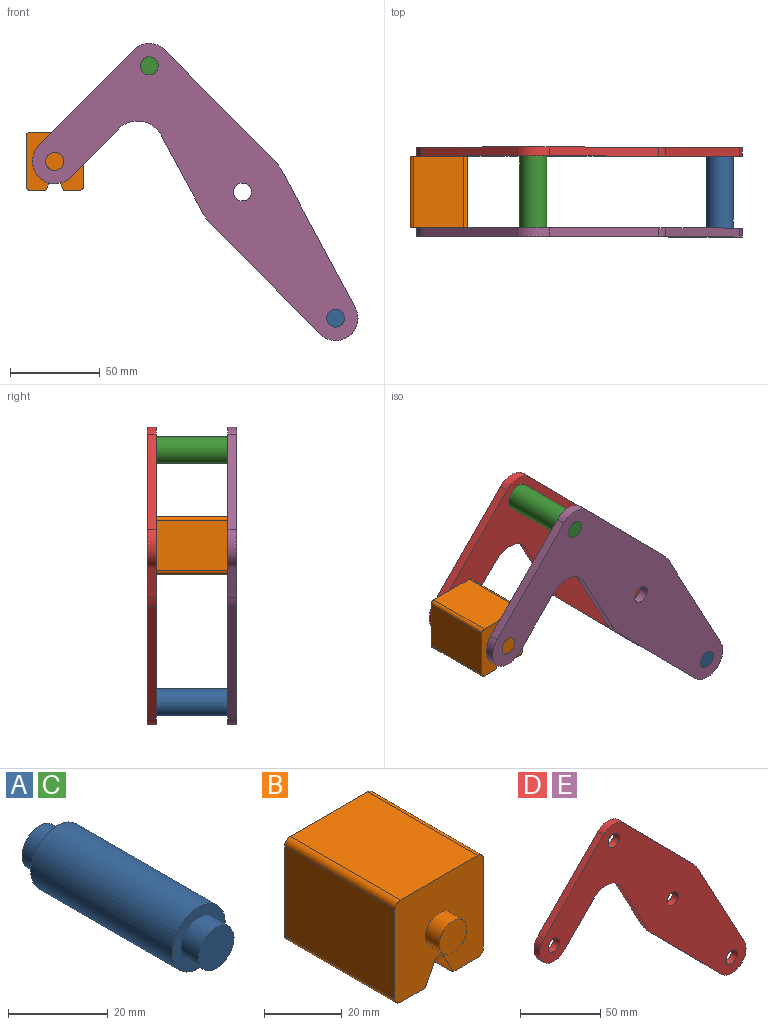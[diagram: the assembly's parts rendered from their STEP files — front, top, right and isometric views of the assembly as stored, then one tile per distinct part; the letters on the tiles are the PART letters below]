
ASSEMBLY  parts=5 mates=3
PART A: 7 faces, bbox 15x50x15 mm
  f0: cylinder r=7.5mm len=40mm, axis (0,-1,0), area 1885mm2, adj f2,f5
  f1: cylinder r=5mm len=10mm, axis (0,1,0), area 157.1mm2, adj f2,f3
  f2: plane 15x15mm, normal (0,-1,0), area 98.2mm2, adj f0,f1
  f3: plane 10x10mm, normal (0,-1,0), area 78.5mm2, adj f1
  f4: cylinder r=5mm len=10mm, axis (0,-1,0), area 157.1mm2, adj f5,f6
  f5: plane 15x15mm, normal (0,1,0), area 98.2mm2, adj f0,f4
  f6: plane 10x10mm, normal (0,1,0), area 78.5mm2, adj f4
PART B: 18 faces, bbox 32.1x50x32.1 mm
  f0: plane 40x28.08mm, normal (1,0,0), area 1123.1mm2, adj f4,f10,f13,f14
  f1: plane 40x9.04mm, normal (0,0,-1), area 361.6mm2, adj f2,f4,f10,f14
  f2: plane 40x6.42mm, normal (-0.89,0,-0.45), area 287.2mm2, adj f1,f4,f10,f15
  f3: plane 40x6.42mm, normal (0.89,0,-0.45), area 287.2mm2, adj f4,f5,f10,f15
  f4: plane 32.08x32.08mm, normal (0,-1,0), area 900.6mm2, adj f0,f1,f2,f3,f5,f6,f7,f9
  f5: plane 40x9.04mm, normal (0,0,-1), area 361.6mm2, adj f3,f4,f10,f16
  f6: plane 40x28.08mm, normal (0,0,1), area 1123.1mm2, adj f4,f10,f13,f17
  f7: plane 40x28.08mm, normal (-1,0,0), area 1123.1mm2, adj f4,f10,f16,f17
  f8: plane 10x10mm, normal (0,-1,0), area 78.5mm2, adj f9
  f9: cylinder r=5mm len=10mm, axis (0,1,0), area 157.1mm2, adj f4,f8
  f10: plane 32.08x32.08mm, normal (0,1,0), area 900.6mm2, adj f0,f1,f2,f3,f5,f6,f7,f12
  f11: plane 10x10mm, normal (0,1,0), area 78.5mm2, adj f12
  f12: cylinder r=5mm len=10mm, axis (0,-1,0), area 157.1mm2, adj f10,f11
  f13: cylinder r=2mm len=40mm, axis (0,1,0), area 125.7mm2, adj f0,f4,f6,f10
  f14: cylinder r=2mm len=40mm, axis (0,-1,0), area 125.7mm2, adj f0,f1,f4,f10
  f15: cylinder r=2mm len=40mm, axis (0,1,0), area 177.1mm2, adj f2,f3,f4,f10
  f16: cylinder r=2mm len=40mm, axis (0,1,0), area 125.7mm2, adj f4,f5,f7,f10
  f17: cylinder r=2mm len=40mm, axis (0,-1,0), area 125.7mm2, adj f4,f6,f7,f10
PART C: same geometry as A
PART D: 18 faces, bbox 181.7x5x165.8 mm
  f0: plane 43.49x23.35mm, normal (-0.88,0,-0.47), area 246.8mm2, adj f1,f14,f16,f17
  f1: cylinder r=25mm len=5.75mm, axis (0,1,0), area 35.8mm2, adj f0,f2,f16,f17
  f2: plane 61.6x60.87mm, normal (-0.71,0,-0.7), area 433mm2, adj f1,f3,f16,f17
  f3: cylinder r=12.5mm len=21.39mm, axis (0,1,0), area 178.4mm2, adj f2,f4,f16,f17
  f4: plane 76.3x40.96mm, normal (0.88,0,0.47), area 433mm2, adj f3,f5,f16,f17
  f5: cylinder r=25mm len=5.75mm, axis (0,1,0), area 35.8mm2, adj f4,f6,f16,f17
  f6: plane 61.6x60.87mm, normal (0.71,0,0.7), area 433mm2, adj f5,f7,f16,f17
  f7: cylinder r=12.5mm len=17.78mm, axis (0,1,0), area 98.9mm2, adj f6,f8,f16,f17
  f8: plane 53.35x52.71mm, normal (-0.71,0,0.7), area 375mm2, adj f7,f9,f16,f17
  f9: cylinder r=12.5mm len=21.39mm, axis (0,1,0), area 196.3mm2, adj f8,f10,f16,f17
  f10: plane 26.86x26.54mm, normal (0.71,0,-0.7), area 188.8mm2, adj f9,f14,f16,f17
  f11: cylinder r=5mm len=10mm, axis (0,1,0), area 157.1mm2, adj f16,f17
  f12: cylinder r=5mm len=10mm, axis (0,1,0), area 157.1mm2, adj f16,f17
  f13: cylinder r=5mm len=10mm, axis (0,1,0), area 157.1mm2, adj f16,f17
  f14: cylinder r=15mm len=23.89mm, axis (0,1,0), area 140.2mm2, adj f0,f10,f16,f17
  f15: cylinder r=5mm len=10mm, axis (0,1,0), area 157.1mm2, adj f16,f17
  f16: plane 181.66x165.78mm, normal (0,-1,0), area 8710.1mm2, adj f0,f1,f2,f3,f4,f5,f6,f7
  f17: plane 181.66x165.78mm, normal (0,1,0), area 8710.1mm2, adj f0,f1,f2,f3,f4,f5,f6,f7
PART E: same geometry as D
PLACE A t=(103.95,-20,-140.78)mm
PLACE B t=(0,-20,0)mm
PLACE C t=(0,-20,0)mm
PLACE D t=(0,25,0)mm
PLACE E t=(0,-20,0)mm fixed
MATE fastened D.f7 <-> C.f0  axis (0,-1,0) through (-51.98,20,70.39)mm
MATE fastened A.f0 <-> E.f3  axis (0,-1,0) through (51.98,-20,-70.39)mm
MATE revolute B.f9 <-> E.f9  axis (0,-1,0) through (-104.69,-20,17.04)mm
